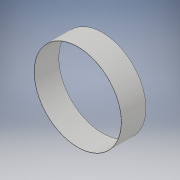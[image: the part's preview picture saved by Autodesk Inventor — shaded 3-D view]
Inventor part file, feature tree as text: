
AUTODESK INVENTOR PART (.ipt)
format: ipt  version: 2019 (Build 230136000, 136)  size: 103,936 bytes
history: native  units: mm
features: extrude x2, sketch x2
ambient origin geometry x8: Origin, YZ Plane, XZ Plane, XY Plane, X Axis, Y Axis, Z Axis, Center Point
bodies: Solid1 (feature_tree)
feature tree (4):
  extrude  "Extrusion1"  Depth=11.65mm TaperAngle=0.0deg
  extrude  "Extrusion2"  Depth=11.65mm TaperAngle=0.0deg
  sketch  "Sketch1"  dims[d0=41.668mm d1=11.65mm d2=0.0mm]
  sketch  "Sketch2"  dims[d3=41.4mm d4=11.65mm d5=0.0mm]
